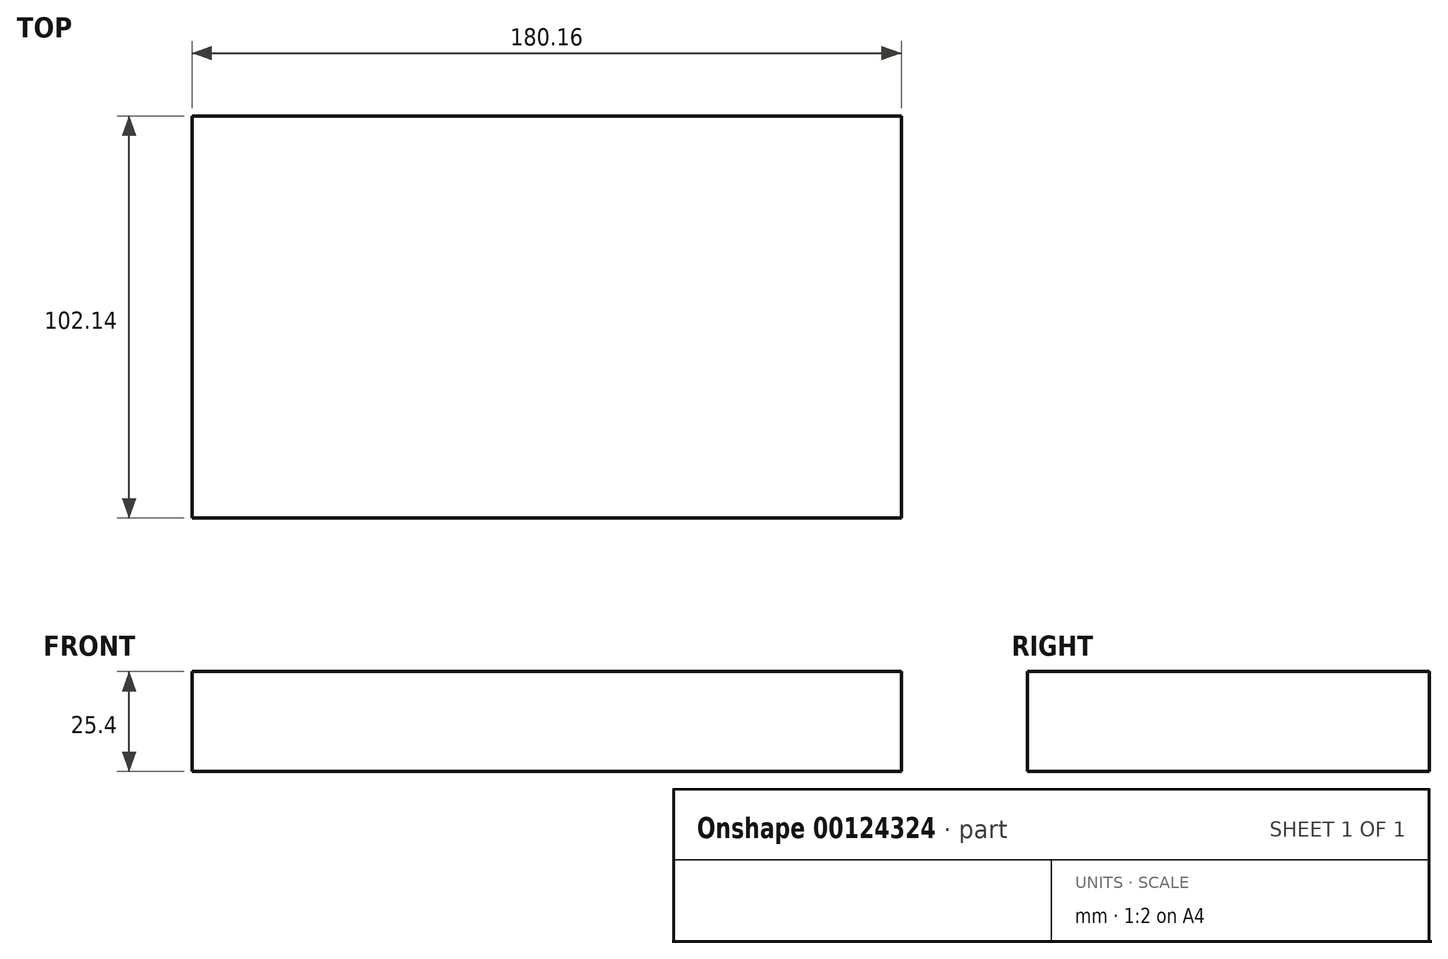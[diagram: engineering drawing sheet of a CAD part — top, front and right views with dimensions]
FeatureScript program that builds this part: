
annotation { "Feature Type Name" : "Feature", "Feature Type Description" : "" }
export const myFeature = defineFeature(function(context is Context, id is Id, definition is map)
    precondition{}
    {
        {
            var Q0;
            Q0=qCreatedBy(makeId("Top.planeOp"),FACE);
            var sketch = newSketch(context, id + "F0", { "sketchPlane" : qUnion([Q0])});
            skLineSegment(sketch, "E0.bottom", {"start": v(90.08, -51.07) * mm, "end": v(-90.08, -51.07) * mm});
            skLineSegment(sketch, "E0.top", {"start": v(90.08, 51.07) * mm, "end": v(-90.08, 51.07) * mm});
            skLineSegment(sketch, "E0.left", {"start": v(90.08, -51.07) * mm, "end": v(90.08, 51.07) * mm});
            skLineSegment(sketch, "E0.right", {"start": v(-90.08, -51.07) * mm, "end": v(-90.08, 51.07) * mm});
            skPoint(sketch, "E0.middle", {"position": v(0, 0) * mm});
            skSolve(sketch);
        }
        {
            var Q0;
            Q0 = qSketchRegion(id + "F0", true);
            extrude(context, id + "F1", {"entities" : qUnion([Q0]), "depth" : 25.4 * mm});
        }
    });
